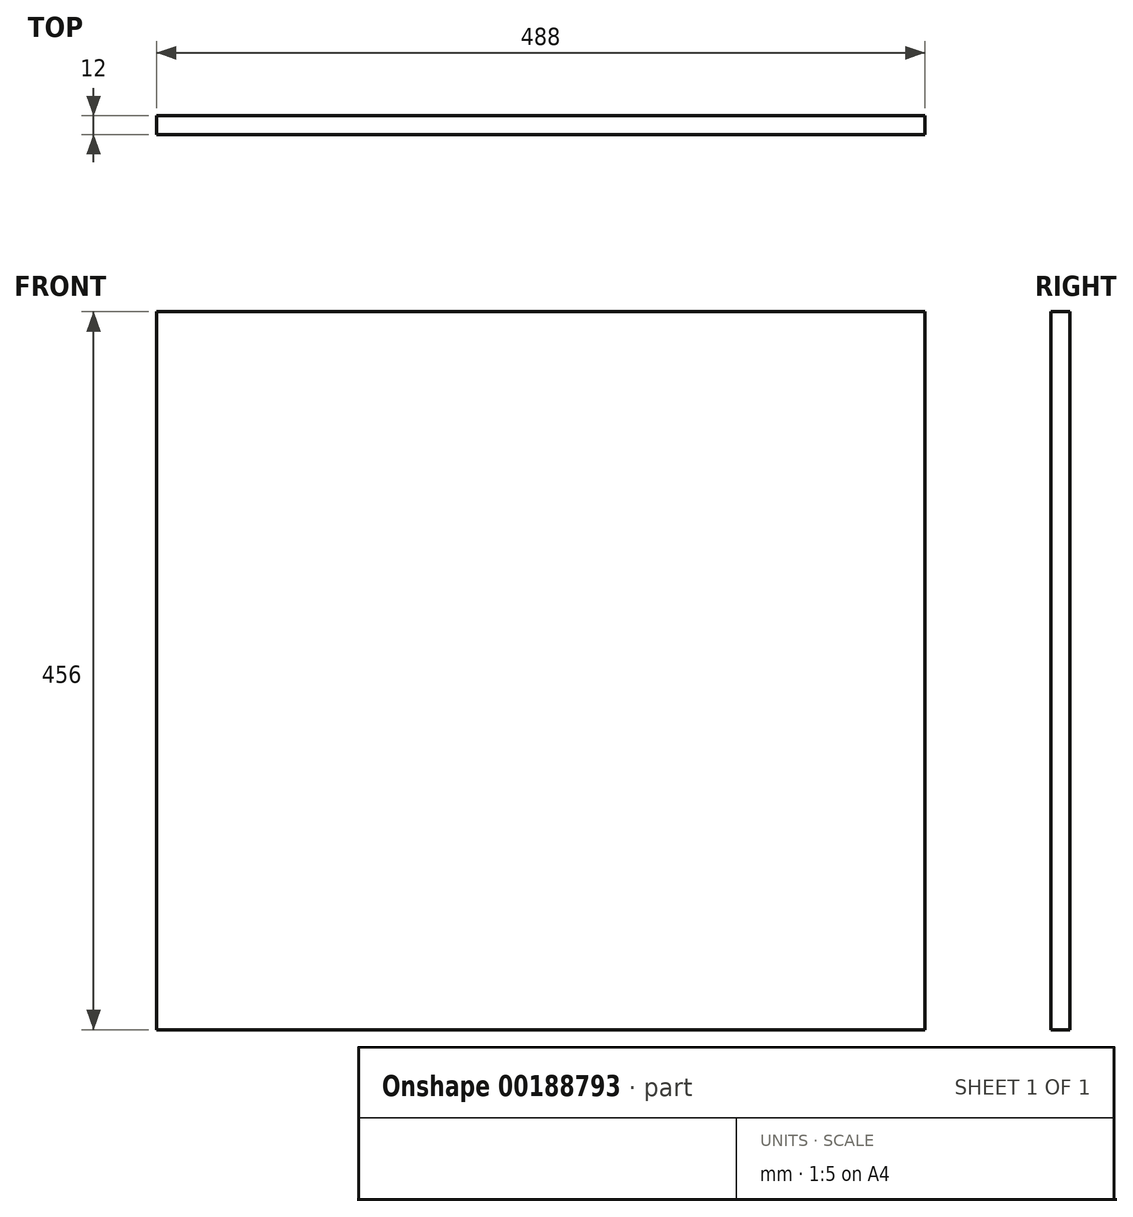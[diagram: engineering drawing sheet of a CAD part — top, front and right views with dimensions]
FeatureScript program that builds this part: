
annotation { "Feature Type Name" : "Feature", "Feature Type Description" : "" }
export const myFeature = defineFeature(function(context is Context, id is Id, definition is map)
    precondition{}
    {
        {
            assignVariable(context, id + "F0", {"name" : "thickness", "anyValue" : 12});
        }
        {
            var Q0;
            Q0=qCreatedBy(makeId("Front.planeOp"),FACE);
            var sketch = newSketch(context, id + "F1", { "sketchPlane" : qUnion([Q0])});
            skLineSegment(sketch, "E0.bottom", {"start": v(244, 228) * mm, "end": v(-244, 228) * mm});
            skLineSegment(sketch, "E0.top", {"start": v(244, -228) * mm, "end": v(-244, -228) * mm});
            skLineSegment(sketch, "E0.left", {"start": v(244, 228) * mm, "end": v(244, -228) * mm});
            skLineSegment(sketch, "E0.right", {"start": v(-244, 228) * mm, "end": v(-244, -228) * mm});
            skPoint(sketch, "E0.middle", {"position": v(0, 0) * mm});
            skSolve(sketch);
        }
        {
            var Q0;
            Q0=makeQuery(id+"F1.imprint","IMPRINT",FACE,{"disambiguationData":[TD([[makeQuery(id+"F1.imprint","IMPRINT",EDGE,{"derivedFrom":sQuery(id+"F1.wireOp",EDGE,"E0.bottom")}),1.0]])]});
            extrude(context, id + "F2", {"entities" : qUnion([Q0]), "depth" : (getVariable(context, 'thickness')) * mm});
        }
    });
